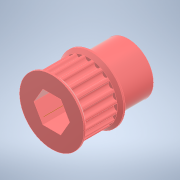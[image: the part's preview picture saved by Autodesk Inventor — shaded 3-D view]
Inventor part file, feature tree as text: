
AUTODESK INVENTOR PART (.ipt)
format: ipt  version: 2022.3 (Build 263350000, 350)  size: 299,520 bytes
history: native  units: in
note: dims shown in document units (in); Inventor stores cm internally (conversion verified against a paired STEP export)
features: extrude x7, sketch x7, mirror x2, chamfer x2, other x1, fillet x1, pattern_circular x1, projected_geometry x1
ambient origin geometry x8: Origin, YZ Plane, XZ Plane, XY Plane, X Axis, Y Axis, Z Axis, Center Point
bodies: Solid1 (feature_tree)
feature tree (22):
  other  "Hex Bore"
  extrude  "HTD Base"  Depth=0.3937in TaperAngle=0.0deg
  extrude  "HTD Flange"  Depth=0.0591in
  mirror  "HTD Flanges"
  chamfer  "HTD Flange Chamfer"  Distance=0.0787in Angle=45.0deg
  extrude  "GT2 Base"  TaperAngle=0.0deg  [1 undecoded]
  extrude  "GT2 Base Tooth"  TaperAngle=0.0deg  [1 undecoded]
  fillet  "GT2 Base Tooth pt. 2"  Radius=0.7219in
  pattern_circular  "GT2 Teeth"  [2 undecoded]
  extrude  "GT2 Flange"  Depth=0.4375in
  mirror  "GT2 Flanges"
  chamfer  "GT2 Flange Chamfer"  Distance=0.0075in
  extrude  "Circle Bore"  TaperAngle=0.0deg  [1 undecoded]
  extrude  "Extrusion9"  Depth=0.0118in
  sketch  "Sketch1"  dims[d0=1.2082in d1=0.3937in d2=0.0in]
  sketch  "Sketch4"  dims[d12=0.0394in d13=0.0591in]
  sketch  "Sketch5"  dims[d14=0.0in]
  sketch  "Sketch6"  dims[d15=0.0394in d16=0.0787in d17=45.0deg]
  sketch  "Sketch7"  dims[d18=0.385in d19=0.0in d20=0.0in]
  sketch  "Sketch8"  dims[d21=0.385in d22=0.0in d23=0.0in d24=0.7219in]
  sketch  "Sketch9"  dims[d25=0.3937in d26=0.0in d27=0.0727in d28=0.0075in d29=0.0in d30=0.0in d31=0.0118in d32=7.874in d33=360.0deg d35=0.0394in d36=0.0591in d37=0.0in d38=0.0394in d39=0.0787in d40=45.0deg d41=0.625in d42=0.4375in d43=0.0in]
  projected_geometry  "Projected Loop1"
note: 5 required parameter values undecoded (feature->parameter linkage not recoverable at this tier; creation-order binding heuristic only, values carry confidence <= 0.55)
